# Revit family: Storage-Multi_Level_Workstations-Teknion-BSSM_Multi-Functional-R2018
name_source: partatom
category: Furniture
revit_build: Autodesk Revit 2018 (Build: 20170223_1515(x64)
units: mm (PartAtom-declared; Revit-internal decimal feet)

## family parameters
Always vertical = Yes
Cut with Voids When Loaded = No
OmniClass Number = 23.40.20.00
OmniClass Title = General Furniture and Specialties
Room Calculation Point = No
Shared = Yes
Work Plane-Based = No

## types (8) — shared parameters
Assembly Code = E2020200
Manufacturer = Teknion
Manufacturer Fax = 416.661.4586
Part Number = BSSM
Product Documentation Link = http://www.teknion.com
Product Line = Expansion Casegoods
Product Page URL = http://www.teknion.com
Series = Expansion Casegoods
Sustainability Data = http://www.teknion.com
URL = www.teknion.com
Unit Weight URL = http://www.teknion.com
Warranty = http://www.teknion.com

## per-type parameters (varying)
| type | Center | Description | End of 1 3/16 inch thick Secondary Desk | End of 1 9/16 inch thick Secondary Desk | End of 1 inch thick Secondary Desk | In Front of Height Adjustable Mechanism | Model |
| Center Position, In Front of Height Adjustable Mechanism, High Secondary Desk | Yes | Multi-Functional Storage for Secondary Desk, Center Position, In Front of Height Adjustable Mechanism, High Secondary Desk | No | No | No | Yes | BSSMCYH_____ |
| End – 1" thick Secondary Desk, In Front of Height Adjustable Mechanism, High Secondary Desk | No | Multi-Functional Storage for Secondary Desk, End – 1" thick Secondary Desk, In Front of Height Adjustable Mechanism, High Secondary Desk | No | No | Yes | Yes | BSSMDYH_____ |
| End – 1 3/16" thick Secondary Desk, In Front of Height Adjustable Mechanism, High Secondary Desk | No | Multi-Functional Storage for Secondary Desk, End – 1 3/16" thick Secondary Desk, In Front of Height Adjustable Mechanism, High Secondary Desk | Yes | No | No | Yes | BSSMMYH_____ |
| End – 1 9/16" thick Secondary Desk, In Front of Height Adjustable Mechanism, High Secondary Desk | No | Multi-Functional Storage for Secondary Desk, End – 1 9/16" thick Secondary Desk, In Front of Height Adjustable Mechanism, High Secondary Desk | No | Yes | No | Yes | BSSMXYH_____ |
| Center Position, High Secondary Desk | Yes | Multi-Functional Storage for Secondary Desk, Center Position, High Secondary Desk | No | No | No | No | BSSMCNH_____ |
| End – 1 3/16" thick Secondary Desk, High Secondary Desk | No | Multi-Functional Storage for Secondary Desk, End – 1 3/16" thick Secondary Desk, High Secondary Desk | Yes | No | No | No | BSSMMNH_____ |
| End – 1 9/16" thick Secondary Desk, High Secondary Desk | No | Multi-Functional Storage for Secondary Desk, End – 1 9/16" thick Secondary Desk, High Secondary Desk | No | Yes | No | No | BSSMXNH_____ |
| End – 1" thick Secondary Desk, High Secondary Desk | No | Multi-Functional Storage for Secondary Desk, End – 1" thick Secondary Desk, High Secondary Desk | No | No | Yes | No | BSSMDNH_____ |

## geometry (parser evidence)
native form markers: Sweep x2
no freeform markers — native parametric forms only
